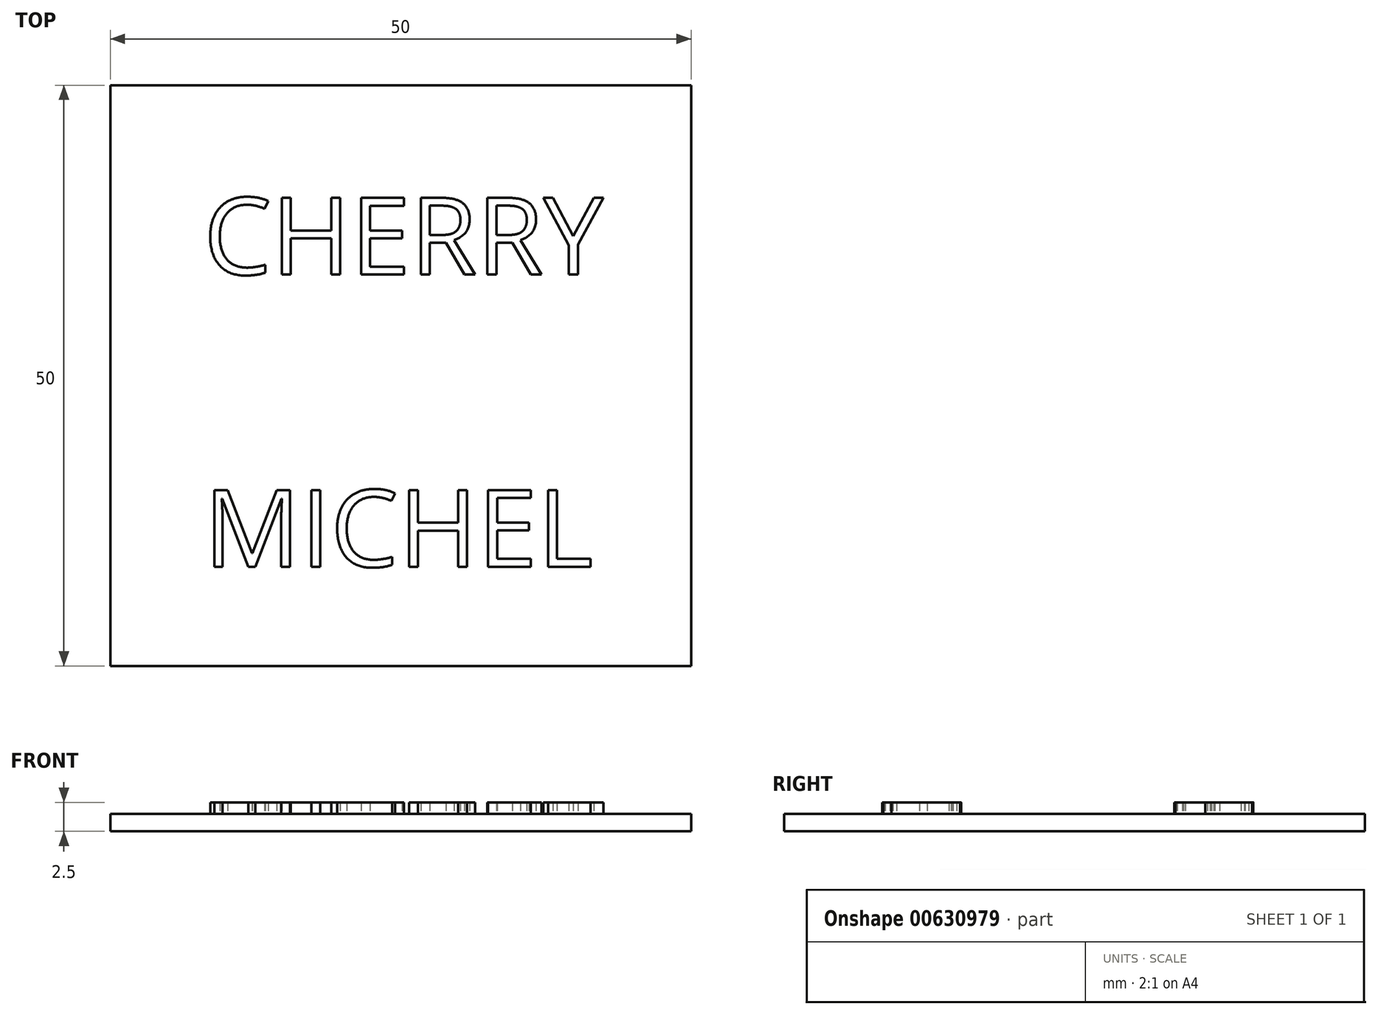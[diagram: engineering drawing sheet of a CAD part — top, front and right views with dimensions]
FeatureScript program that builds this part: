
annotation { "Feature Type Name" : "Feature", "Feature Type Description" : "" }
export const myFeature = defineFeature(function(context is Context, id is Id, definition is map)
    precondition{}
    {
        {
            var Q0;
            Q0=qCreatedBy(makeId("Top.planeOp"),FACE);
            var sketch = newSketch(context, id + "F0", { "sketchPlane" : qUnion([Q0])});
            skLineSegment(sketch, "E0.bottom", {"start": v(25, -25) * mm, "end": v(-25, -25) * mm});
            skLineSegment(sketch, "E0.top", {"start": v(25, 25) * mm, "end": v(-25, 25) * mm});
            skLineSegment(sketch, "E0.left", {"start": v(25, -25) * mm, "end": v(25, 25) * mm});
            skLineSegment(sketch, "E0.right", {"start": v(-25, -25) * mm, "end": v(-25, 25) * mm});
            skPoint(sketch, "E0.middle", {"position": v(0, 0) * mm});
            skSolve(sketch);
        }
        {
            var Q0;
            Q0=makeQuery(id+"F0.imprint","IMPRINT",FACE,{"disambiguationData":[TD([[makeQuery(id+"F0.imprint","IMPRINT",EDGE,{"derivedFrom":sQuery(id+"F0.wireOp",EDGE,"E0.bottom")}),-1.0]])]});
            extrude(context, id + "F1", {"entities" : qUnion([Q0]), "depth" : 1.5 * mm, "offsetDistance" : 25 * mm});
        }
        {
            var Q0;
            Q0=makeQuery(id+"F1.opExtrude","CAP_FACE",FACE,{"disambiguationData":[OSD([sQuery(id+"F0.wireOp",EDGE,"E0.bottom"),sQuery(id+"F0.wireOp",EDGE,"E0.top"),sQuery(id+"F0.wireOp",EDGE,"E0.left"),sQuery(id+"F0.wireOp",EDGE,"E0.right")])],"isStart":false});
            var sketch = newSketch(context, id + "F2", { "sketchPlane" : qUnion([Q0])});
            skText(sketch, "E1", { "text": "CHERRY\n\nMICHEL", "fontName": "OpenSans-Regular.ttf"});
            const initialGuessF2  = {"E1": [-0.01697, 0.0087, 1, 0, 0.00666]};
            skSetInitialGuess(sketch, initialGuessF2);
            skSolve(sketch);
        }
        {
            var Q0;
            Q0 = qSketchRegion(id + "F2", true);
            extrude(context, id + "F3", {"entities" : qUnion([Q0]), "operationType" : NewBodyOperationType.ADD, "depth" : 1 * mm, "offsetDistance" : 25 * mm});
        }
    });
